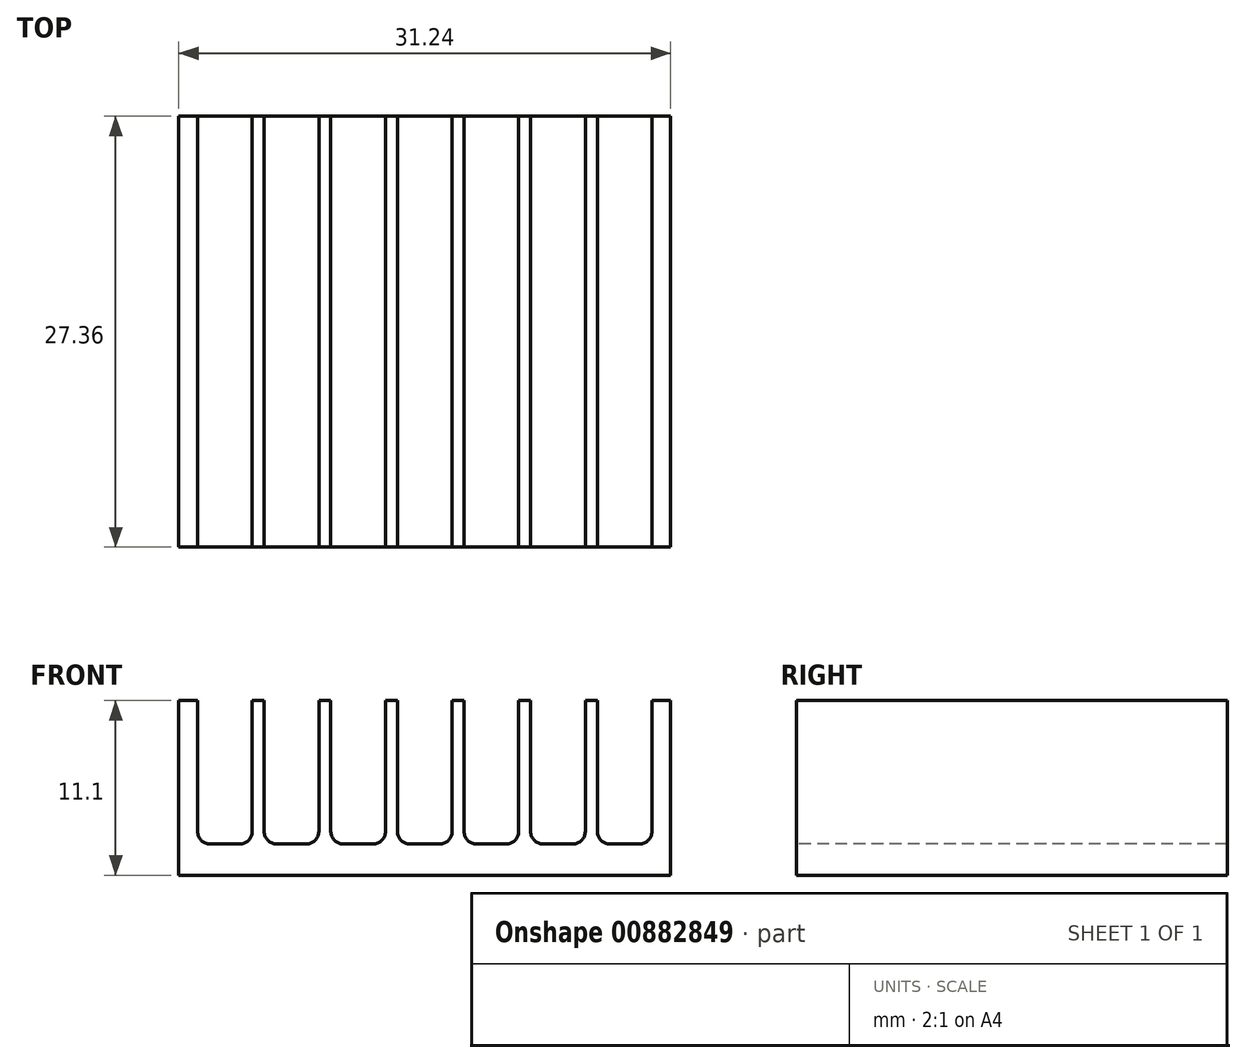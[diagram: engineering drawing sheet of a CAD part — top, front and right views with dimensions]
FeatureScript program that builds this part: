
annotation { "Feature Type Name" : "Feature", "Feature Type Description" : "" }
export const myFeature = defineFeature(function(context is Context, id is Id, definition is map)
    precondition{}
    {
        {
            var Q0;
            Q0=qCreatedBy(makeId("Front.planeOp"),FACE);
            var sketch = newSketch(context, id + "F0", { "sketchPlane" : qUnion([Q0])});
            skLineSegment(sketch, "E0.bottom", {"start": v(0, 11.1) * mm, "end": v(31.24, 11.1) * mm});
            skLineSegment(sketch, "E0.top", {"start": v(0, 0) * mm, "end": v(31.24, 0) * mm});
            skLineSegment(sketch, "E0.left", {"start": v(0, 11.1) * mm, "end": v(0, 0) * mm});
            skLineSegment(sketch, "E0.right", {"start": v(31.24, 11.1) * mm, "end": v(31.24, 0) * mm});
            skSolve(sketch);
        }
        {
            var Q0;
            Q0 = qSketchRegion(id + "F0", true);
            extrude(context, id + "F1", {"entities" : qUnion([Q0]), "depth" : 27.36 * mm, "offsetDistance" : 25.4 * mm});
        }
        {
            var Q0;
            Q0=makeQuery(id+"F1.opExtrude","CAP_FACE",FACE,{"disambiguationData":[OSD([sQuery(id+"F0.wireOp",EDGE,"E0.bottom"),sQuery(id+"F0.wireOp",EDGE,"E0.top"),sQuery(id+"F0.wireOp",EDGE,"E0.left"),sQuery(id+"F0.wireOp",EDGE,"E0.right")])],"isStart":false});
            var sketch = newSketch(context, id + "F2", { "sketchPlane" : qUnion([Q0])});
            skLineSegment(sketch, "E1.bottom", {"start": v(30.05, 11.1) * mm, "end": v(26.58, 11.1) * mm});
            skLineSegment(sketch, "E1.top", {"start": v(30.05, 1.98) * mm, "end": v(26.58, 1.98) * mm});
            skLineSegment(sketch, "E1.left", {"start": v(30.05, 11.1) * mm, "end": v(30.05, 1.98) * mm});
            skLineSegment(sketch, "E1.right", {"start": v(26.58, 11.1) * mm, "end": v(26.58, 1.98) * mm});
            skLineSegment(sketch, "E2.bottom", {"start": v(25.82, 11.1) * mm, "end": v(22.35, 11.1) * mm});
            skLineSegment(sketch, "E2.top", {"start": v(25.82, 1.98) * mm, "end": v(22.35, 1.98) * mm});
            skLineSegment(sketch, "E2.left", {"start": v(25.82, 11.1) * mm, "end": v(25.82, 1.98) * mm});
            skLineSegment(sketch, "E2.right", {"start": v(22.35, 11.1) * mm, "end": v(22.35, 1.98) * mm});
            skLineSegment(sketch, "E3.bottom", {"start": v(21.59, 11.1) * mm, "end": v(18.12, 11.1) * mm});
            skLineSegment(sketch, "E3.top", {"start": v(21.59, 1.98) * mm, "end": v(18.12, 1.98) * mm});
            skLineSegment(sketch, "E3.left", {"start": v(21.59, 11.1) * mm, "end": v(21.59, 1.98) * mm});
            skLineSegment(sketch, "E3.right", {"start": v(18.12, 11.1) * mm, "end": v(18.12, 1.98) * mm});
            skLineSegment(sketch, "E4.bottom", {"start": v(17.36, 11.1) * mm, "end": v(13.89, 11.1) * mm});
            skLineSegment(sketch, "E4.top", {"start": v(17.36, 1.98) * mm, "end": v(13.89, 1.98) * mm});
            skLineSegment(sketch, "E4.left", {"start": v(17.36, 11.1) * mm, "end": v(17.36, 1.98) * mm});
            skLineSegment(sketch, "E4.right", {"start": v(13.89, 11.1) * mm, "end": v(13.89, 1.98) * mm});
            skLineSegment(sketch, "E5.bottom", {"start": v(13.12, 11.1) * mm, "end": v(9.66, 11.1) * mm});
            skLineSegment(sketch, "E5.top", {"start": v(13.12, 1.98) * mm, "end": v(9.66, 1.98) * mm});
            skLineSegment(sketch, "E5.left", {"start": v(13.12, 11.1) * mm, "end": v(13.12, 1.98) * mm});
            skLineSegment(sketch, "E5.right", {"start": v(9.66, 11.1) * mm, "end": v(9.66, 1.98) * mm});
            skLineSegment(sketch, "E6.bottom", {"start": v(8.9, 11.1) * mm, "end": v(5.42, 11.1) * mm});
            skLineSegment(sketch, "E6.top", {"start": v(8.9, 1.98) * mm, "end": v(5.42, 1.98) * mm});
            skLineSegment(sketch, "E6.left", {"start": v(8.9, 11.1) * mm, "end": v(8.9, 1.98) * mm});
            skLineSegment(sketch, "E6.right", {"start": v(5.42, 11.1) * mm, "end": v(5.42, 1.98) * mm});
            skLineSegment(sketch, "E7.bottom", {"start": v(4.66, 11.1) * mm, "end": v(1.2, 11.1) * mm});
            skLineSegment(sketch, "E7.top", {"start": v(4.66, 1.98) * mm, "end": v(1.2, 1.98) * mm});
            skLineSegment(sketch, "E7.left", {"start": v(4.66, 11.1) * mm, "end": v(4.66, 1.98) * mm});
            skLineSegment(sketch, "E7.right", {"start": v(1.2, 11.1) * mm, "end": v(1.2, 1.98) * mm});
            skSolve(sketch);
        }
        {
            var Q0;
            Q0=makeQuery(id+"F2.imprint","IMPRINT",FACE,{"disambiguationData":[TD([[makeQuery(id+"F2.imprint","IMPRINT",EDGE,{"derivedFrom":sQuery(id+"F2.wireOp",EDGE,"E7.bottom")}),-1.0]])]});
            var Q1;
            Q1=makeQuery(id+"F2.imprint","IMPRINT",FACE,{"disambiguationData":[TD([[makeQuery(id+"F2.imprint","IMPRINT",EDGE,{"derivedFrom":sQuery(id+"F2.wireOp",EDGE,"E6.bottom")}),-1.0]])]});
            var Q2;
            Q2=makeQuery(id+"F2.imprint","IMPRINT",FACE,{"disambiguationData":[TD([[makeQuery(id+"F2.imprint","IMPRINT",EDGE,{"derivedFrom":sQuery(id+"F2.wireOp",EDGE,"E5.bottom")}),-1.0]])]});
            var Q3;
            Q3=makeQuery(id+"F2.imprint","IMPRINT",FACE,{"disambiguationData":[TD([[makeQuery(id+"F2.imprint","IMPRINT",EDGE,{"derivedFrom":sQuery(id+"F2.wireOp",EDGE,"E4.bottom")}),-1.0]])]});
            var Q4;
            Q4=makeQuery(id+"F2.imprint","IMPRINT",FACE,{"disambiguationData":[TD([[makeQuery(id+"F2.imprint","IMPRINT",EDGE,{"derivedFrom":sQuery(id+"F2.wireOp",EDGE,"E3.bottom")}),-1.0]])]});
            var Q5;
            Q5=makeQuery(id+"F2.imprint","IMPRINT",FACE,{"disambiguationData":[TD([[makeQuery(id+"F2.imprint","IMPRINT",EDGE,{"derivedFrom":sQuery(id+"F2.wireOp",EDGE,"E2.bottom")}),-1.0]])]});
            var Q6;
            Q6=makeQuery(id+"F2.imprint","IMPRINT",FACE,{"disambiguationData":[TD([[makeQuery(id+"F2.imprint","IMPRINT",EDGE,{"derivedFrom":sQuery(id+"F2.wireOp",EDGE,"E1.bottom")}),-1.0]])]});
            extrude(context, id + "F3", {"entities" : qUnion([Q0, Q1, Q2, Q3, Q4, Q5, Q6]), "operationType" : NewBodyOperationType.REMOVE, "endBound" : BoundingType.THROUGH_ALL, "oppositeDirection" : true, "depth" : 25.4 * mm, "offsetDistance" : 25.4 * mm});
        }
        {
            var Q0;
            Q0=makeQuery(id+"F3.boolean.opBoolean","COPY",EDGE,{"derivedFrom":makeQuery(id+"F3.opExtrude","SWEPT_EDGE",EDGE,{"disambiguationData":[OSD([sQuery(id+"F2.wireOp",EDGE,"E7.top"),sQuery(id+"F2.wireOp",EDGE,"E7.right")])]})});
            var Q1;
            Q1=makeQuery(id+"F3.boolean.opBoolean","COPY",EDGE,{"derivedFrom":makeQuery(id+"F3.opExtrude","SWEPT_EDGE",EDGE,{"disambiguationData":[OSD([sQuery(id+"F2.wireOp",EDGE,"E7.top"),sQuery(id+"F2.wireOp",EDGE,"E7.left")])]})});
            var Q2;
            Q2=makeQuery(id+"F3.boolean.opBoolean","COPY",EDGE,{"derivedFrom":makeQuery(id+"F3.opExtrude","SWEPT_EDGE",EDGE,{"disambiguationData":[OSD([sQuery(id+"F2.wireOp",EDGE,"E6.top"),sQuery(id+"F2.wireOp",EDGE,"E6.right")])]})});
            var Q3;
            Q3=makeQuery(id+"F3.boolean.opBoolean","COPY",EDGE,{"derivedFrom":makeQuery(id+"F3.opExtrude","SWEPT_EDGE",EDGE,{"disambiguationData":[OSD([sQuery(id+"F2.wireOp",EDGE,"E6.top"),sQuery(id+"F2.wireOp",EDGE,"E6.left")])]})});
            var Q4;
            Q4=makeQuery(id+"F3.boolean.opBoolean","COPY",EDGE,{"derivedFrom":makeQuery(id+"F3.opExtrude","SWEPT_EDGE",EDGE,{"disambiguationData":[OSD([sQuery(id+"F2.wireOp",EDGE,"E5.top"),sQuery(id+"F2.wireOp",EDGE,"E5.right")])]})});
            var Q5;
            Q5=makeQuery(id+"F3.boolean.opBoolean","COPY",EDGE,{"derivedFrom":makeQuery(id+"F3.opExtrude","SWEPT_EDGE",EDGE,{"disambiguationData":[OSD([sQuery(id+"F2.wireOp",EDGE,"E5.top"),sQuery(id+"F2.wireOp",EDGE,"E5.left")])]})});
            var Q6;
            Q6=makeQuery(id+"F3.boolean.opBoolean","COPY",EDGE,{"derivedFrom":makeQuery(id+"F3.opExtrude","SWEPT_EDGE",EDGE,{"disambiguationData":[OSD([sQuery(id+"F2.wireOp",EDGE,"E4.top"),sQuery(id+"F2.wireOp",EDGE,"E4.right")])]})});
            var Q7;
            Q7=makeQuery(id+"F3.boolean.opBoolean","COPY",EDGE,{"derivedFrom":makeQuery(id+"F3.opExtrude","SWEPT_EDGE",EDGE,{"disambiguationData":[OSD([sQuery(id+"F2.wireOp",EDGE,"E4.top"),sQuery(id+"F2.wireOp",EDGE,"E4.left")])]})});
            var Q8;
            Q8=makeQuery(id+"F3.boolean.opBoolean","COPY",EDGE,{"derivedFrom":makeQuery(id+"F3.opExtrude","SWEPT_EDGE",EDGE,{"disambiguationData":[OSD([sQuery(id+"F2.wireOp",EDGE,"E3.top"),sQuery(id+"F2.wireOp",EDGE,"E3.right")])]})});
            var Q9;
            Q9=makeQuery(id+"F3.boolean.opBoolean","COPY",EDGE,{"derivedFrom":makeQuery(id+"F3.opExtrude","SWEPT_EDGE",EDGE,{"disambiguationData":[OSD([sQuery(id+"F2.wireOp",EDGE,"E3.top"),sQuery(id+"F2.wireOp",EDGE,"E3.left")])]})});
            var Q10;
            Q10=makeQuery(id+"F3.boolean.opBoolean","COPY",EDGE,{"derivedFrom":makeQuery(id+"F3.opExtrude","SWEPT_EDGE",EDGE,{"disambiguationData":[OSD([sQuery(id+"F2.wireOp",EDGE,"E2.top"),sQuery(id+"F2.wireOp",EDGE,"E2.right")])]})});
            var Q11;
            Q11=makeQuery(id+"F3.boolean.opBoolean","COPY",EDGE,{"derivedFrom":makeQuery(id+"F3.opExtrude","SWEPT_EDGE",EDGE,{"disambiguationData":[OSD([sQuery(id+"F2.wireOp",EDGE,"E2.top"),sQuery(id+"F2.wireOp",EDGE,"E2.left")])]})});
            var Q12;
            Q12=makeQuery(id+"F3.boolean.opBoolean","COPY",EDGE,{"derivedFrom":makeQuery(id+"F3.opExtrude","SWEPT_EDGE",EDGE,{"disambiguationData":[OSD([sQuery(id+"F2.wireOp",EDGE,"E1.top"),sQuery(id+"F2.wireOp",EDGE,"E1.right")])]})});
            var Q13;
            Q13=makeQuery(id+"F3.boolean.opBoolean","COPY",EDGE,{"derivedFrom":makeQuery(id+"F3.opExtrude","SWEPT_EDGE",EDGE,{"disambiguationData":[OSD([sQuery(id+"F2.wireOp",EDGE,"E1.top"),sQuery(id+"F2.wireOp",EDGE,"E1.left")])]})});
            fillet(context, id + "F4", {"entities" : qUnion([Q0, Q1, Q2, Q3, Q4, Q5, Q6, Q7, Q8, Q9, Q10, Q11, Q12, Q13]), "radius" : 0.8 * mm, "allowEdgeOverflow" : false});
        }
    });
